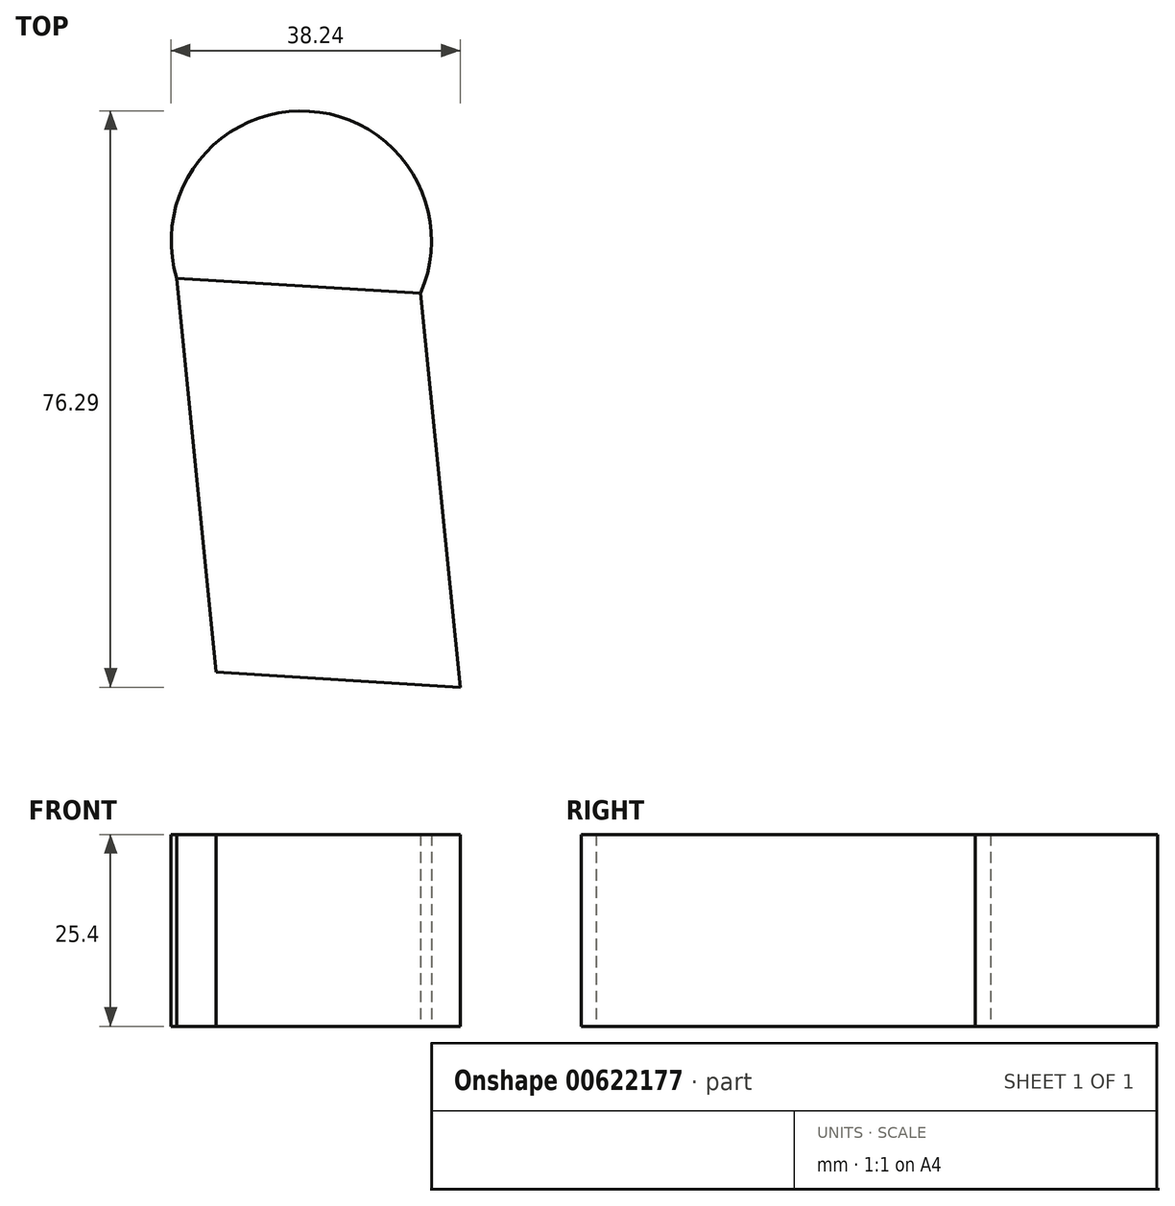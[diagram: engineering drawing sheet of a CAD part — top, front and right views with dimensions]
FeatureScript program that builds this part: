
annotation { "Feature Type Name" : "Feature", "Feature Type Description" : "" }
export const myFeature = defineFeature(function(context is Context, id is Id, definition is map)
    precondition{}
    {
        {
            var Q0;
            Q0=qCreatedBy(makeId("Top.planeOp"),FACE);
            var sketch = newSketch(context, id + "F0", { "sketchPlane" : qUnion([Q0])});
            skLineSegment(sketch, "E0", {"start": v(-49.39, 22.18) * mm, "end": v(-17.08, 20.19) * mm});
            skLineSegment(sketch, "E1", {"start": v(-28.02, -31) * mm, "end": v(45.53, -33.48) * mm});
            skLineSegment(sketch, "E2", {"start": v(45.53, -33.48) * mm, "end": v(-49.88, -51.37) * mm});
            skArc(sketch, "E3", {"start": v(-17.08, 20.19) * mm, "mid": v(-31.81, 44.27) * mm, "end": v(-49.39, 22.18) * mm});
            skLineSegment(sketch, "E4", {"start": v(-28.02, -31) * mm, "end": v(-33.23, 21.18) * mm});
            skFitSpline(sketch, "E5", {"points": [v(-49.39, 22.18) * mm, v(-64.87, 5.53) * mm, v(-57.4, -29.6) * mm, v(-57.64, -29.6) * mm, v(-57.64, -29.36) * mm], "startDerivative": vector(-54.25, -25.96) * mm, "endDerivative": vector(1.88, 6.5) * mm});
            skSolve(sketch);
        }
        {
            var Q0;
            Q0=makeQuery(id+"F0.imprint","IMPRINT",FACE,{"disambiguationData":[TD([[makeQuery(id+"F0.imprint","IMPRINT",EDGE,{"derivedFrom":sQuery(id+"F0.wireOp",EDGE,"E0")}),1.0]])]});
            extrude(context, id + "F1", {"entities" : qUnion([Q0]), "depth" : 25.4 * mm, "offsetDistance" : 25.4 * mm});
        }
        {
            var Q0;
            Q0=makeQuery(id+"F1.opExtrude","SWEPT_FACE",FACE,{"disambiguationData":[OSD([sQuery(id+"F0.wireOp",EDGE,"E0")])]});
            var Q1;
            Q1=sQuery(id+"F0.wireOp",EDGE,"E4");
            sweep(context, id + "F2", {"profiles" : qUnion([Q0]), "path" : qUnion([Q1])});
        }
    });
